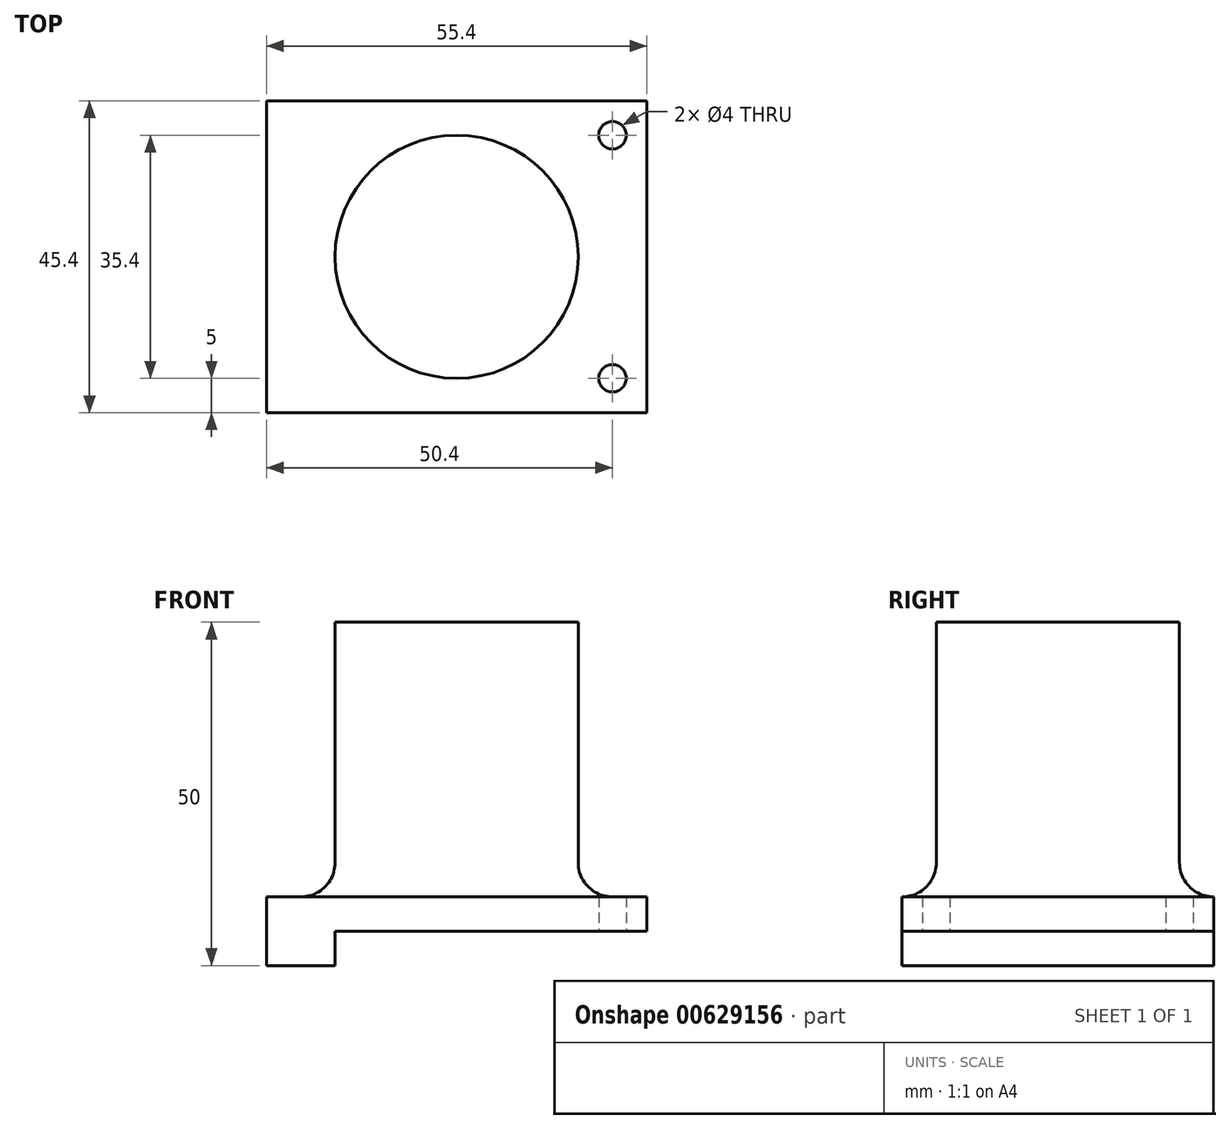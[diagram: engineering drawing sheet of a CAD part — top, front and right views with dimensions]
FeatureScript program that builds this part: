
annotation { "Feature Type Name" : "Feature", "Feature Type Description" : "" }
export const myFeature = defineFeature(function(context is Context, id is Id, definition is map)
    precondition{}
    {
        {
            var Q0;
            Q0=qCreatedBy(makeId("Top.planeOp"),FACE);
            var sketch = newSketch(context, id + "F0", { "sketchPlane" : qUnion([Q0])});
            skCircle(sketch, "E0", {"center": v(0, 0) * mm, "radius": 17.7 * mm});
            skLineSegment(sketch, "E1.bottom", {"start": v(-27.7, 22.7) * mm, "end": v(27.7, 22.7) * mm});
            skLineSegment(sketch, "E1.top", {"start": v(-27.7, -22.7) * mm, "end": v(27.7, -22.7) * mm});
            skLineSegment(sketch, "E1.left", {"start": v(-27.7, 22.7) * mm, "end": v(-27.7, -22.7) * mm});
            skLineSegment(sketch, "E1.right", {"start": v(27.7, 22.7) * mm, "end": v(27.7, -22.7) * mm});
            skLineSegment(sketch, "E2", {"start": v(-17.7, 22.7) * mm, "end": v(-17.7, -22.7) * mm});
            skCircle(sketch, "E3", {"center": v(22.7, 17.7) * mm, "radius": 2 * mm});
            skLineSegment(sketch, "E4", {"start": v(27.7, 0) * mm, "end": v(17.7, 0) * mm, "construction": true});
            skCircle(sketch, "E5.MirrorC", {"center": v(22.7, -17.7) * mm, "radius": 2 * mm});
            skSolve(sketch);
        }
        {
            var Q0;
            {var subQ6=sQuery(id+"F0.wireOp",EDGE,"E0");Q0=makeQuery(id+"F0.imprint","IMPRINT",FACE,{"disambiguationData":[TD([[makeQuery(id+"F0.imprint","IMPRINT",EDGE,{"derivedFrom":subQ6}),-1.0]])]});}
            var Q1;
            Q1=makeQuery(id+"F0.imprint","IMPRINT",FACE,{"disambiguationData":[TD([[makeQuery(id+"F0.imprint","IMPRINT",EDGE,{"derivedFrom":sQuery(id+"F0.wireOp",EDGE,"E0")}),1.0]])]});
            extrude(context, id + "F1", {"entities" : qUnion([Q0, Q1]), "depth" : 5 * mm, "offsetDistance" : 25 * mm});
        }
        {
            var Q0;
            Q0=makeQuery(id+"F0.imprint","IMPRINT",FACE,{"disambiguationData":[TD([[makeQuery(id+"F0.imprint","IMPRINT",EDGE,{"derivedFrom":sQuery(id+"F0.wireOp",EDGE,"E0")}),1.0]])]});
            extrude(context, id + "F2", {"entities" : qUnion([Q0]), "operationType" : NewBodyOperationType.ADD, "depth" : 45 * mm, "offsetDistance" : 25 * mm});
        }
        {
            var Q0;
            {var subQ4=sQuery(id+"F0.wireOp",EDGE,"E1.left");Q0=makeQuery(id+"F0.imprint","IMPRINT",FACE,{"disambiguationData":[TD([[makeQuery(id+"F0.imprint","IMPRINT",EDGE,{"derivedFrom":subQ4}),1.0]])]});}
            var Q1;
            Q1=makeQuery(id+"F1.opExtrude","CAP_FACE",FACE,{"disambiguationData":[OSD([sQuery(id+"F0.wireOp",EDGE,"E1.bottom"),sQuery(id+"F0.wireOp",EDGE,"E1.top"),sQuery(id+"F0.wireOp",EDGE,"E1.right"),sQuery(id+"F0.wireOp",EDGE,"E2"),sQuery(id+"F0.wireOp",EDGE,"E3"),sQuery(id+"F0.wireOp",EDGE,"E5.MirrorC")])],"isStart":false});
            extrude(context, id + "F3", {"entities" : qUnion([Q0]), "operationType" : NewBodyOperationType.ADD, "endBound" : BoundingType.UP_TO_SURFACE, "depth" : 25 * mm, "endBoundEntityFace" : qUnion([Q1]), "offsetDistance" : 25 * mm});
        }
        {
            var Q0;
            {var subQ4=sQuery(id+"F0.wireOp",EDGE,"E1.left");Q0=makeQuery(id+"F0.imprint","IMPRINT",FACE,{"disambiguationData":[TD([[makeQuery(id+"F0.imprint","IMPRINT",EDGE,{"derivedFrom":subQ4}),1.0]])]});}
            extrude(context, id + "F4", {"entities" : qUnion([Q0]), "operationType" : NewBodyOperationType.ADD, "oppositeDirection" : true, "depth" : 5 * mm, "offsetDistance" : 25 * mm});
        }
        {
            var Q0;
            Q0=makeQuery(id+"F2.boolean.opBoolean","INTERSECT",EDGE,{"derivedFrom":[makeQuery(id+"F1.opExtrude","CAP_FACE",FACE,{"disambiguationData":[OSD([sQuery(id+"F0.wireOp",EDGE,"E1.bottom"),sQuery(id+"F0.wireOp",EDGE,"E1.top"),sQuery(id+"F0.wireOp",EDGE,"E1.right"),sQuery(id+"F0.wireOp",EDGE,"E2"),sQuery(id+"F0.wireOp",EDGE,"E3"),sQuery(id+"F0.wireOp",EDGE,"E5.MirrorC")])],"isStart":false}),makeQuery(id+"F2.opExtrude","SWEPT_FACE",FACE,{"disambiguationData":[OSD([sQuery(id+"F0.wireOp",EDGE,"E0")])]})]});
            fillet(context, id + "F5", {"entities" : qUnion([Q0]), "radius" : 5 * mm, "tangentPropagation" : true, "allowEdgeOverflow" : false});
        }
    });
